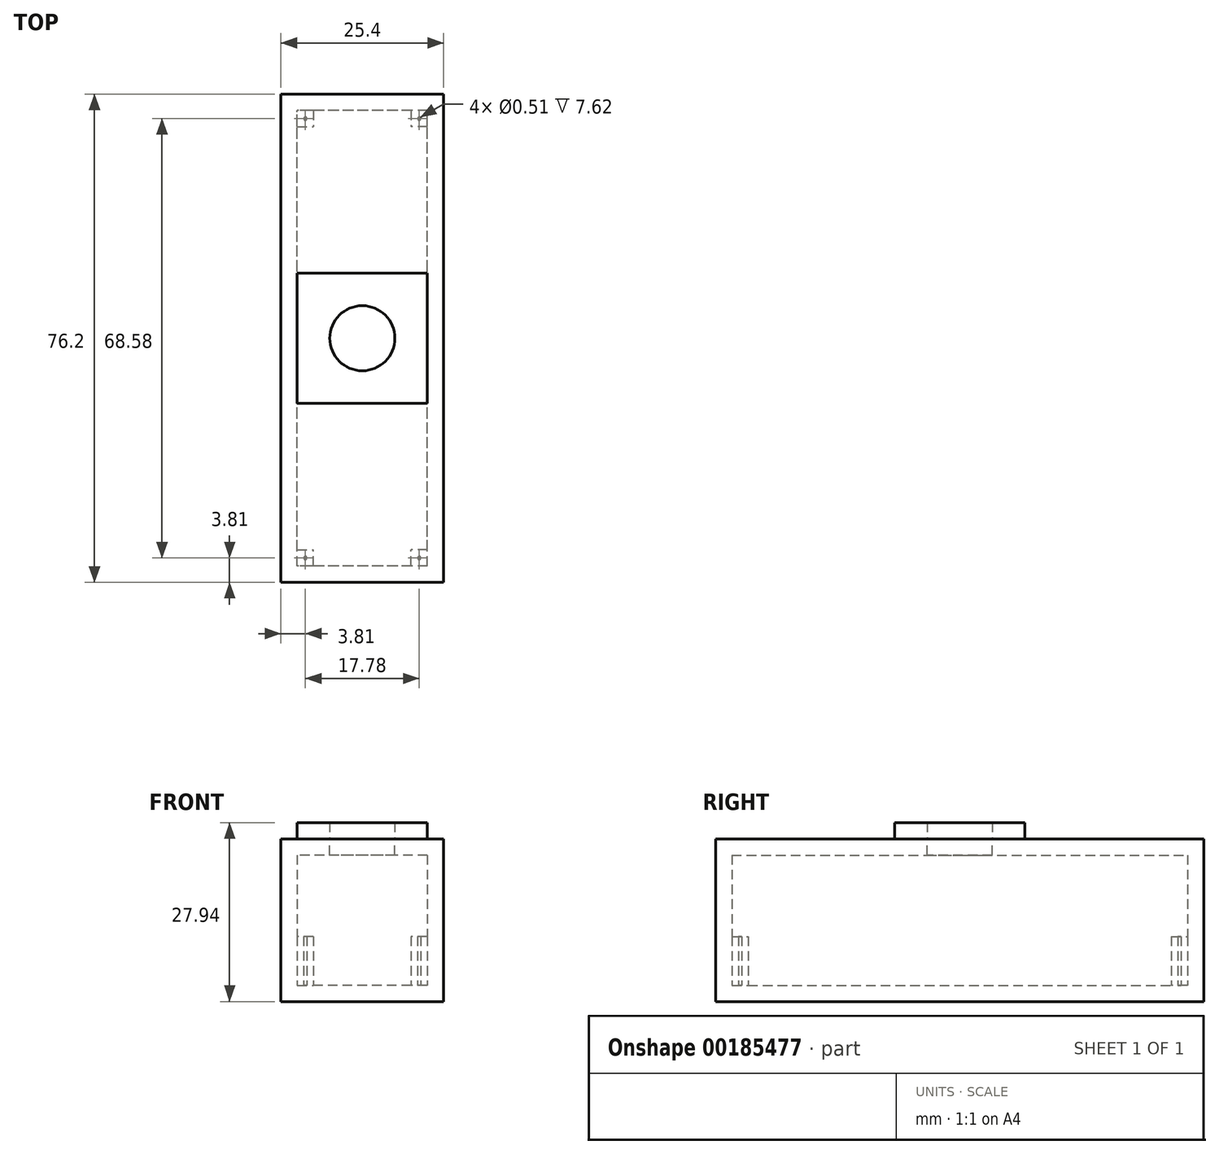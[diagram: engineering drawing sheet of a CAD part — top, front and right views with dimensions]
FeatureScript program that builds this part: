
annotation { "Feature Type Name" : "Feature", "Feature Type Description" : "" }
export const myFeature = defineFeature(function(context is Context, id is Id, definition is map)
    precondition{}
    {
        {
            var Q0;
            Q0=qCreatedBy(makeId("Front.planeOp"),FACE);
            var sketch = newSketch(context, id + "F0", { "sketchPlane" : qUnion([Q0])});
            skLineSegment(sketch, "E0.bottom", {"start": v(12.7, 12.7) * mm, "end": v(-12.7, 12.7) * mm});
            skLineSegment(sketch, "E0.top", {"start": v(12.7, -12.7) * mm, "end": v(-12.7, -12.7) * mm});
            skLineSegment(sketch, "E0.left", {"start": v(12.7, 12.7) * mm, "end": v(12.7, -12.7) * mm});
            skLineSegment(sketch, "E0.right", {"start": v(-12.7, 12.7) * mm, "end": v(-12.7, -12.7) * mm});
            skPoint(sketch, "E0.middle", {"position": v(0, 0) * mm});
            skSolve(sketch);
        }
        {
            var Q0;
            Q0=makeQuery(id+"F0.imprint","IMPRINT",FACE,{"disambiguationData":[TD([[makeQuery(id+"F0.imprint","IMPRINT",EDGE,{"derivedFrom":sQuery(id+"F0.wireOp",EDGE,"E0.bottom")}),1.0]])]});
            extrude(context, id + "F1", {"entities" : qUnion([Q0]), "endBound" : BoundingType.SYMMETRIC, "depth" : 76.2 * mm});
        }
        {
            var Q0;
            Q0=makeQuery(id+"F1.opExtrude","SWEPT_FACE",FACE,{"disambiguationData":[OSD([sQuery(id+"F0.wireOp",EDGE,"E0.right")])]});
            var Q1;
            Q1=makeQuery(id+"F1.opExtrude","SWEPT_BODY",BODY,{"disambiguationData":[OSD([sQuery(id+"F0.wireOp",EDGE,"E0.bottom"),sQuery(id+"F0.wireOp",EDGE,"E0.top"),sQuery(id+"F0.wireOp",EDGE,"E0.left"),sQuery(id+"F0.wireOp",EDGE,"E0.right")])]});
            shell(context, id + "F2", {"isHollow" : true, "entities" : qUnion([Q0]), "parts" : qUnion([Q1]), "thickness" : 2.54 * mm});
        }
        {
            var Q0;
            Q0=makeQuery(id+"F1.opExtrude","SWEPT_FACE",FACE,{"disambiguationData":[OSD([sQuery(id+"F0.wireOp",EDGE,"E0.bottom")])]});
            var sketch = newSketch(context, id + "F3", { "sketchPlane" : qUnion([Q0])});
            skLineSegment(sketch, "E1.bottom", {"start": v(10.16, 10.16) * mm, "end": v(-10.16, 10.16) * mm});
            skLineSegment(sketch, "E1.top", {"start": v(10.16, -10.16) * mm, "end": v(-10.16, -10.16) * mm});
            skLineSegment(sketch, "E1.left", {"start": v(10.16, 10.16) * mm, "end": v(10.16, -10.16) * mm});
            skLineSegment(sketch, "E1.right", {"start": v(-10.16, 10.16) * mm, "end": v(-10.16, -10.16) * mm});
            skPoint(sketch, "E1.middle", {"position": v(0, 0) * mm});
            skCircle(sketch, "E2", {"center": v(0, 0) * mm, "radius": 5.08 * mm});
            skSolve(sketch);
        }
        {
            var Q0;
            Q0=makeQuery(id+"F3.imprint","IMPRINT",FACE,{"disambiguationData":[TD([[makeQuery(id+"F3.imprint","IMPRINT",EDGE,{"derivedFrom":sQuery(id+"F3.wireOp",EDGE,"E2")}),1.0]])]});
            extrude(context, id + "F4", {"entities" : qUnion([Q0]), "operationType" : NewBodyOperationType.REMOVE, "oppositeDirection" : true, "depth" : 2.54 * mm});
        }
        {
            var Q0;
            Q0 = qSketchRegion(id + "F3", true);
            extrude(context, id + "F5", {"entities" : qUnion([Q0]), "depth" : 2.54 * mm});
        }
        {
            var Q0;
            Q0=makeQuery(id+"F2.opShell","OFFSET_FACE",FACE,{"disambiguationData":[OSD([sQuery(id+"F0.wireOp",EDGE,"E0.top")])]});
            var sketch = newSketch(context, id + "F6", { "sketchPlane" : qUnion([Q0])});
            skLineSegment(sketch, "E3.bottom", {"start": v(-10.16, 35.56) * mm, "end": v(-7.62, 35.56) * mm});
            skLineSegment(sketch, "E3.top", {"start": v(-10.16, 33.02) * mm, "end": v(-7.62, 33.02) * mm});
            skLineSegment(sketch, "E3.left", {"start": v(-10.16, 35.56) * mm, "end": v(-10.16, 33.02) * mm});
            skLineSegment(sketch, "E3.right", {"start": v(-7.62, 35.56) * mm, "end": v(-7.62, 33.02) * mm});
            skLineSegment(sketch, "E4.bottom", {"start": v(10.16, 35.56) * mm, "end": v(7.62, 35.56) * mm});
            skLineSegment(sketch, "E4.top", {"start": v(10.16, 33.02) * mm, "end": v(7.62, 33.02) * mm});
            skLineSegment(sketch, "E4.left", {"start": v(10.16, 35.56) * mm, "end": v(10.16, 33.02) * mm});
            skLineSegment(sketch, "E4.right", {"start": v(7.62, 35.56) * mm, "end": v(7.62, 33.02) * mm});
            skLineSegment(sketch, "E5.bottom", {"start": v(10.16, -35.56) * mm, "end": v(7.62, -35.56) * mm});
            skLineSegment(sketch, "E5.top", {"start": v(10.16, -33.02) * mm, "end": v(7.62, -33.02) * mm});
            skLineSegment(sketch, "E5.left", {"start": v(10.16, -35.56) * mm, "end": v(10.16, -33.02) * mm});
            skLineSegment(sketch, "E5.right", {"start": v(7.62, -35.56) * mm, "end": v(7.62, -33.02) * mm});
            skLineSegment(sketch, "E6.bottom", {"start": v(-10.16, -35.56) * mm, "end": v(-7.62, -35.56) * mm});
            skLineSegment(sketch, "E6.top", {"start": v(-10.16, -33.02) * mm, "end": v(-7.62, -33.02) * mm});
            skLineSegment(sketch, "E6.left", {"start": v(-10.16, -35.56) * mm, "end": v(-10.16, -33.02) * mm});
            skLineSegment(sketch, "E6.right", {"start": v(-7.62, -35.56) * mm, "end": v(-7.62, -33.02) * mm});
            skPoint(sketch, "E7", {"position": v(-8.9, 34.3) * mm});
            skPoint(sketch, "E8", {"position": v(-8.9, -34.3) * mm});
            skPoint(sketch, "E9", {"position": v(8.9, -34.3) * mm});
            skPoint(sketch, "E10", {"position": v(8.9, 34.3) * mm});
            skCircle(sketch, "E11", {"center": v(-8.9, -34.3) * mm, "radius": 0.25 * mm});
            skCircle(sketch, "E12", {"center": v(8.9, -34.3) * mm, "radius": 0.25 * mm});
            skCircle(sketch, "E13", {"center": v(8.9, 34.3) * mm, "radius": 0.25 * mm});
            skCircle(sketch, "E14", {"center": v(-8.9, 34.3) * mm, "radius": 0.25 * mm});
            skSolve(sketch);
        }
        {
            var Q0;
            Q0=makeQuery(id+"F6.imprint","IMPRINT",FACE,{"disambiguationData":[TD([[makeQuery(id+"F6.imprint","IMPRINT",EDGE,{"derivedFrom":sQuery(id+"F6.wireOp",EDGE,"E3.bottom")}),1.0]])]});
            var Q1;
            Q1=makeQuery(id+"F6.imprint","IMPRINT",FACE,{"disambiguationData":[TD([[makeQuery(id+"F6.imprint","IMPRINT",EDGE,{"derivedFrom":sQuery(id+"F6.wireOp",EDGE,"E4.bottom")}),1.0]])]});
            var Q2;
            Q2=makeQuery(id+"F6.imprint","IMPRINT",FACE,{"disambiguationData":[TD([[makeQuery(id+"F6.imprint","IMPRINT",EDGE,{"derivedFrom":sQuery(id+"F6.wireOp",EDGE,"E5.bottom")}),-1.0]])]});
            var Q3;
            Q3=makeQuery(id+"F6.imprint","IMPRINT",FACE,{"disambiguationData":[TD([[makeQuery(id+"F6.imprint","IMPRINT",EDGE,{"derivedFrom":sQuery(id+"F6.wireOp",EDGE,"E6.bottom")}),-1.0]])]});
            extrude(context, id + "F7", {"entities" : qUnion([Q0, Q1, Q2, Q3]), "operationType" : NewBodyOperationType.ADD, "depth" : 7.62 * mm});
        }
    });
